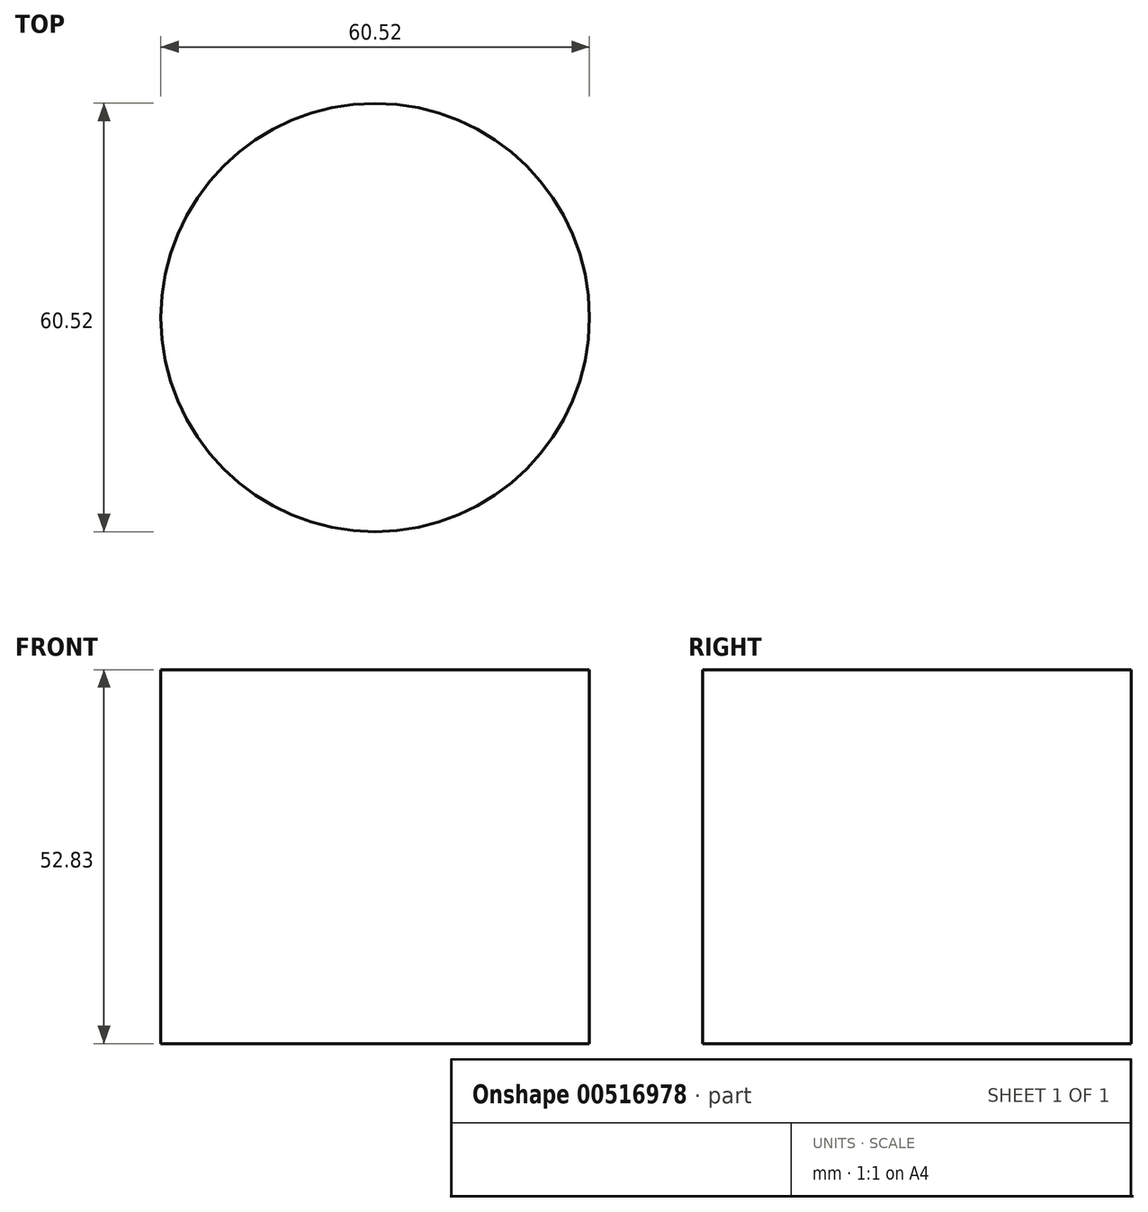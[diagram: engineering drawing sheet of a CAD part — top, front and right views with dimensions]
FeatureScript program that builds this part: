
annotation { "Feature Type Name" : "Feature", "Feature Type Description" : "" }
export const myFeature = defineFeature(function(context is Context, id is Id, definition is map)
    precondition{}
    {
        {
            var Q0;
            Q0=qCreatedBy(makeId("Top.planeOp"),FACE);
            var sketch = newSketch(context, id + "F0", { "sketchPlane" : qUnion([Q0])});
            skCircle(sketch, "E0", {"center": v(0, 0) * mm, "radius": 30.26 * mm});
            skSolve(sketch);
        }
        {
            var Q0;
            Q0 = qSketchRegion(id + "F0", true);
            extrude(context, id + "F1", {"entities" : qUnion([Q0]), "depth" : 52.83 * mm, "offsetDistance" : 25.4 * mm});
        }
    });
